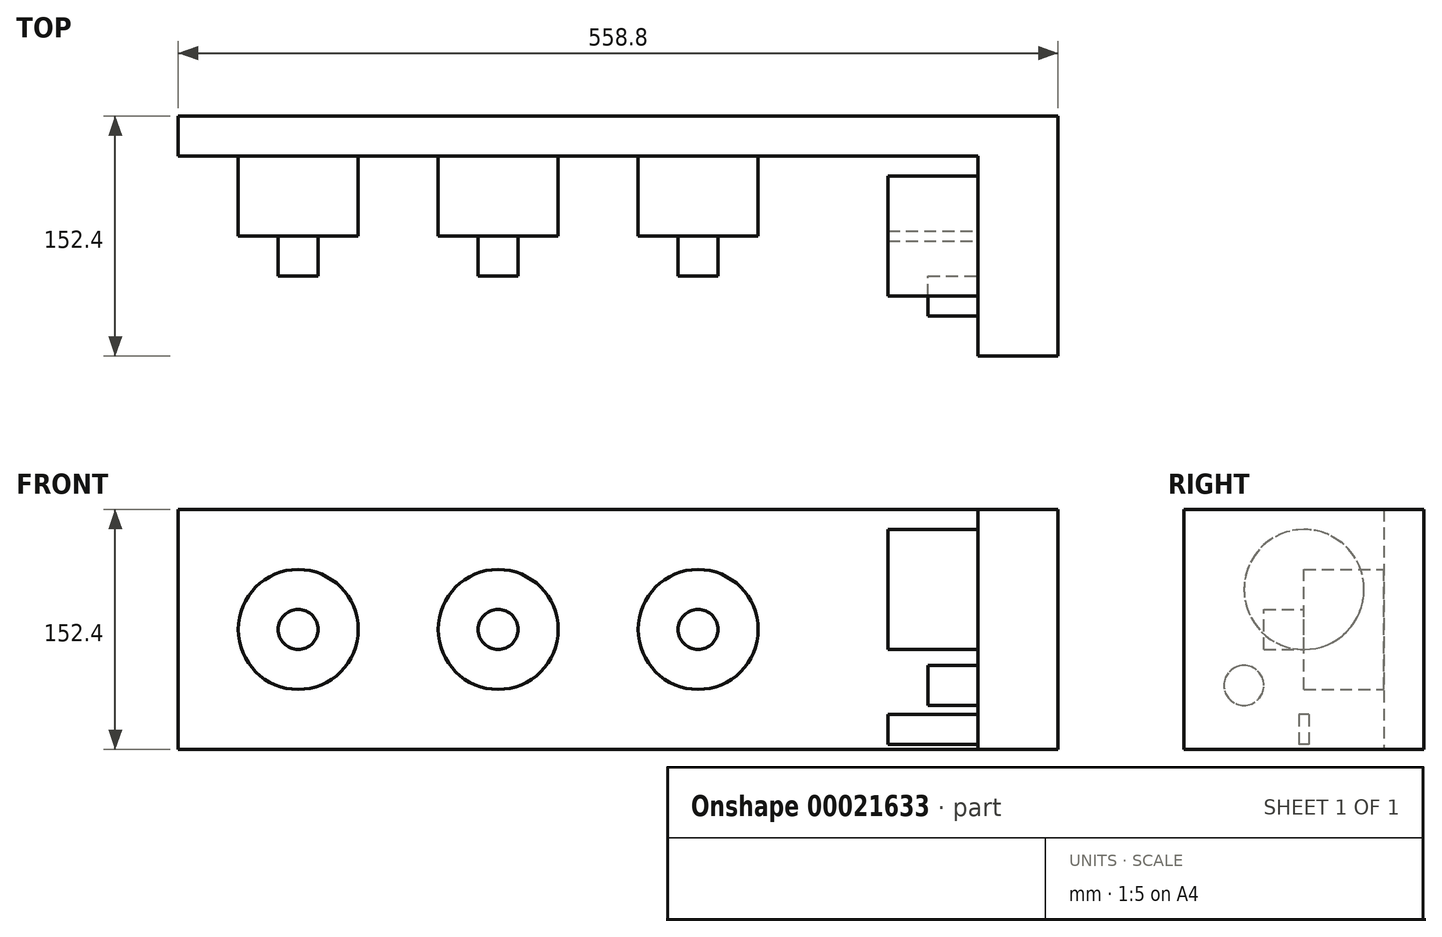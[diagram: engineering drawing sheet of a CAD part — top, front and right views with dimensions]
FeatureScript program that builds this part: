
annotation { "Feature Type Name" : "Feature", "Feature Type Description" : "" }
export const myFeature = defineFeature(function(context is Context, id is Id, definition is map)
    precondition{}
    {
        {
            var Q0;
            Q0=qCreatedBy(makeId("Front.planeOp"),FACE);
            var sketch = newSketch(context, id + "F0", { "sketchPlane" : qUnion([Q0])});
            skLineSegment(sketch, "E0.bottom", {"start": v(-417.16, -3.43) * mm, "end": v(141.64, -3.43) * mm});
            skLineSegment(sketch, "E0.top", {"start": v(-417.16, -155.83) * mm, "end": v(141.64, -155.83) * mm});
            skLineSegment(sketch, "E0.left", {"start": v(-417.16, -3.43) * mm, "end": v(-417.16, -155.83) * mm});
            skLineSegment(sketch, "E0.right", {"start": v(141.64, -3.43) * mm, "end": v(141.64, -155.83) * mm});
            skPoint(sketch, "E1", {"position": v(90.84, -3.43) * mm});
            skLineSegment(sketch, "E2", {"start": v(90.84, -3.43) * mm, "end": v(90.84, -155.83) * mm});
            skPoint(sketch, "E3", {"position": v(27.34, -3.43) * mm});
            skPoint(sketch, "E4", {"position": v(-340.96, -3.43) * mm});
            skPoint(sketch, "E5", {"position": v(-213.96, -3.43) * mm});
            skPoint(sketch, "E6", {"position": v(-86.96, -3.43) * mm});
            skLineSegment(sketch, "E7", {"start": v(-86.96, -3.43) * mm, "end": v(-86.96, -155.83) * mm, "construction": true});
            skCircle(sketch, "E8", {"center": v(-86.96, -79.63) * mm, "radius": 12.7 * mm});
            skCircle(sketch, "E9", {"center": v(-86.96, -79.63) * mm, "radius": 38.1 * mm});
            skLineSegment(sketch, "E10", {"start": v(-340.96, -3.43) * mm, "end": v(-340.96, -155.83) * mm, "construction": true});
            skCircle(sketch, "E11", {"center": v(-340.96, -79.63) * mm, "radius": 12.7 * mm});
            skCircle(sketch, "E12", {"center": v(-340.96, -79.63) * mm, "radius": 38.1 * mm});
            skLineSegment(sketch, "E13", {"start": v(-213.96, -3.43) * mm, "end": v(-213.96, -155.83) * mm, "construction": true});
            skCircle(sketch, "E14", {"center": v(-213.96, -79.63) * mm, "radius": 12.7 * mm});
            skCircle(sketch, "E15", {"center": v(-213.96, -79.63) * mm, "radius": 38.1 * mm});
            skSolve(sketch);
        }
        {
            var Q0;
            {var subQ1=sQuery(id+"F0.wireOp",EDGE,"E0.left");Q0=makeQuery(id+"F0.imprint","IMPRINT",FACE,{"disambiguationData":[TD([[makeQuery(id+"F0.imprint","IMPRINT",EDGE,{"derivedFrom":subQ1}),1.0]])]});}
            extrude(context, id + "F1", {"entities" : qUnion([Q0]), "depth" : 25.4 * mm});
        }
        {
            var Q0;
            Q0=makeQuery(id+"F0.imprint","IMPRINT",FACE,{"disambiguationData":[TD([[makeQuery(id+"F0.imprint","IMPRINT",EDGE,{"derivedFrom":sQuery(id+"F0.wireOp",EDGE,"4705e8f3-8c40-45a6-b7f0-81be4bd91c47")}),1.0]])]});
            var Q1;
            Q1=makeQuery(id+"F0.imprint","IMPRINT",FACE,{"disambiguationData":[TD([[makeQuery(id+"F0.imprint","IMPRINT",EDGE,{"derivedFrom":sQuery(id+"F0.wireOp",EDGE,"7870bddb-49f4-4078-ae8d-6e39b9749376")}),-1.0]])]});
            var Q2;
            Q2=makeQuery(id+"F0.imprint","IMPRINT",FACE,{"disambiguationData":[TD([[makeQuery(id+"F0.imprint","IMPRINT",EDGE,{"derivedFrom":sQuery(id+"F0.wireOp",EDGE,"E8")}),-1.0]])]});
            var Q3;
            Q3=makeQuery(id+"F0.imprint","IMPRINT",FACE,{"disambiguationData":[TD([[makeQuery(id+"F0.imprint","IMPRINT",EDGE,{"derivedFrom":sQuery(id+"F0.wireOp",EDGE,"E14")}),-1.0]])]});
            var Q4;
            Q4=makeQuery(id+"F0.imprint","IMPRINT",FACE,{"disambiguationData":[TD([[makeQuery(id+"F0.imprint","IMPRINT",EDGE,{"derivedFrom":sQuery(id+"F0.wireOp",EDGE,"E11")}),-1.0]])]});
            extrude(context, id + "F2", {"entities" : qUnion([Q0, Q1, Q2, Q3, Q4]), "operationType" : NewBodyOperationType.ADD, "depth" : 76.2 * mm});
        }
        {
            var Q0;
            Q0=makeQuery(id+"F0.imprint","IMPRINT",FACE,{"disambiguationData":[TD([[makeQuery(id+"F0.imprint","IMPRINT",EDGE,{"derivedFrom":sQuery(id+"F0.wireOp",EDGE,"7870bddb-49f4-4078-ae8d-6e39b9749376")}),1.0]])]});
            var Q1;
            Q1=makeQuery(id+"F0.imprint","IMPRINT",FACE,{"disambiguationData":[TD([[makeQuery(id+"F0.imprint","IMPRINT",EDGE,{"derivedFrom":sQuery(id+"F0.wireOp",EDGE,"E8")}),1.0]])]});
            var Q2;
            Q2=makeQuery(id+"F0.imprint","IMPRINT",FACE,{"disambiguationData":[TD([[makeQuery(id+"F0.imprint","IMPRINT",EDGE,{"derivedFrom":sQuery(id+"F0.wireOp",EDGE,"3bae0637-7d53-447b-bcc2-1e1bf928f10d")}),1.0]])]});
            var Q3;
            Q3=makeQuery(id+"F0.imprint","IMPRINT",FACE,{"disambiguationData":[TD([[makeQuery(id+"F0.imprint","IMPRINT",EDGE,{"derivedFrom":sQuery(id+"F0.wireOp",EDGE,"E14")}),1.0]])]});
            var Q4;
            Q4=makeQuery(id+"F0.imprint","IMPRINT",FACE,{"disambiguationData":[TD([[makeQuery(id+"F0.imprint","IMPRINT",EDGE,{"derivedFrom":sQuery(id+"F0.wireOp",EDGE,"E11")}),1.0]])]});
            extrude(context, id + "F3", {"entities" : qUnion([Q0, Q1, Q2, Q3, Q4]), "operationType" : NewBodyOperationType.ADD, "depth" : 101.6 * mm});
        }
        {
            var Q0;
            {var subQ1=sQuery(id+"F0.wireOp",EDGE,"E0.right");Q0=makeQuery(id+"F0.imprint","IMPRINT",FACE,{"disambiguationData":[TD([[makeQuery(id+"F0.imprint","IMPRINT",EDGE,{"derivedFrom":subQ1}),-1.0]])]});}
            extrude(context, id + "F4", {"entities" : qUnion([Q0]), "operationType" : NewBodyOperationType.ADD, "depth" : 152.4 * mm});
        }
        {
            var Q0;
            Q0=makeQuery(id+"F4.opExtrude","SWEPT_FACE",FACE,{"disambiguationData":[OSD([sQuery(id+"F0.wireOp",EDGE,"E2")])]});
            var sketch = newSketch(context, id + "F5", { "sketchPlane" : qUnion([Q0])});
            skPoint(sketch, "E16", {"position": v(76.2, -3.43) * mm});
            skPoint(sketch, "E17", {"position": v(114.3, -3.43) * mm});
            skLineSegment(sketch, "E18", {"start": v(76.2, -3.43) * mm, "end": v(76.2, -155.83) * mm, "construction": true});
            skPoint(sketch, "E19", {"position": v(76.2, -54.23) * mm});
            skCircle(sketch, "E20", {"center": v(76.2, -54.23) * mm, "radius": 38.1 * mm});
            skLineSegment(sketch, "E21", {"start": v(114.3, -5.56) * mm, "end": v(114.3, -155.83) * mm, "construction": true});
            skLineSegment(sketch, "E22.rect.bottom", {"start": v(73.03, -133.6) * mm, "end": v(79.38, -133.6) * mm});
            skLineSegment(sketch, "E22.rect.top", {"start": v(73.03, -152.65) * mm, "end": v(79.38, -152.65) * mm});
            skLineSegment(sketch, "E22.rect.left", {"start": v(73.03, -133.6) * mm, "end": v(73.03, -152.65) * mm});
            skLineSegment(sketch, "E22.rect.right", {"start": v(79.38, -133.6) * mm, "end": v(79.38, -152.65) * mm});
            skPoint(sketch, "E22.rect.middle", {"position": v(76.2, -143.13) * mm});
            skCircle(sketch, "E23", {"center": v(114.3, -115.19) * mm, "radius": 12.7 * mm});
            skSolve(sketch);
        }
        {
            var Q0;
            Q0=makeQuery(id+"F5.imprint","IMPRINT",FACE,{"disambiguationData":[TD([[makeQuery(id+"F5.imprint","IMPRINT",EDGE,{"derivedFrom":sQuery(id+"F5.wireOp",EDGE,"E20")}),1.0]])]});
            var Q1;
            Q1=makeQuery(id+"F5.imprint","IMPRINT",FACE,{"disambiguationData":[TD([[makeQuery(id+"F5.imprint","IMPRINT",EDGE,{"derivedFrom":sQuery(id+"F5.wireOp",EDGE,"E22.rect.bottom")}),-1.0]])]});
            extrude(context, id + "F6", {"entities" : qUnion([Q0, Q1]), "operationType" : NewBodyOperationType.ADD, "depth" : 57.15 * mm});
        }
        {
            var Q0;
            Q0=makeQuery(id+"F5.imprint","IMPRINT",FACE,{"disambiguationData":[TD([[makeQuery(id+"F5.imprint","IMPRINT",EDGE,{"derivedFrom":sQuery(id+"F5.wireOp",EDGE,"E23")}),1.0]])]});
            extrude(context, id + "F7", {"entities" : qUnion([Q0]), "operationType" : NewBodyOperationType.ADD, "depth" : 31.75 * mm});
        }
    });
